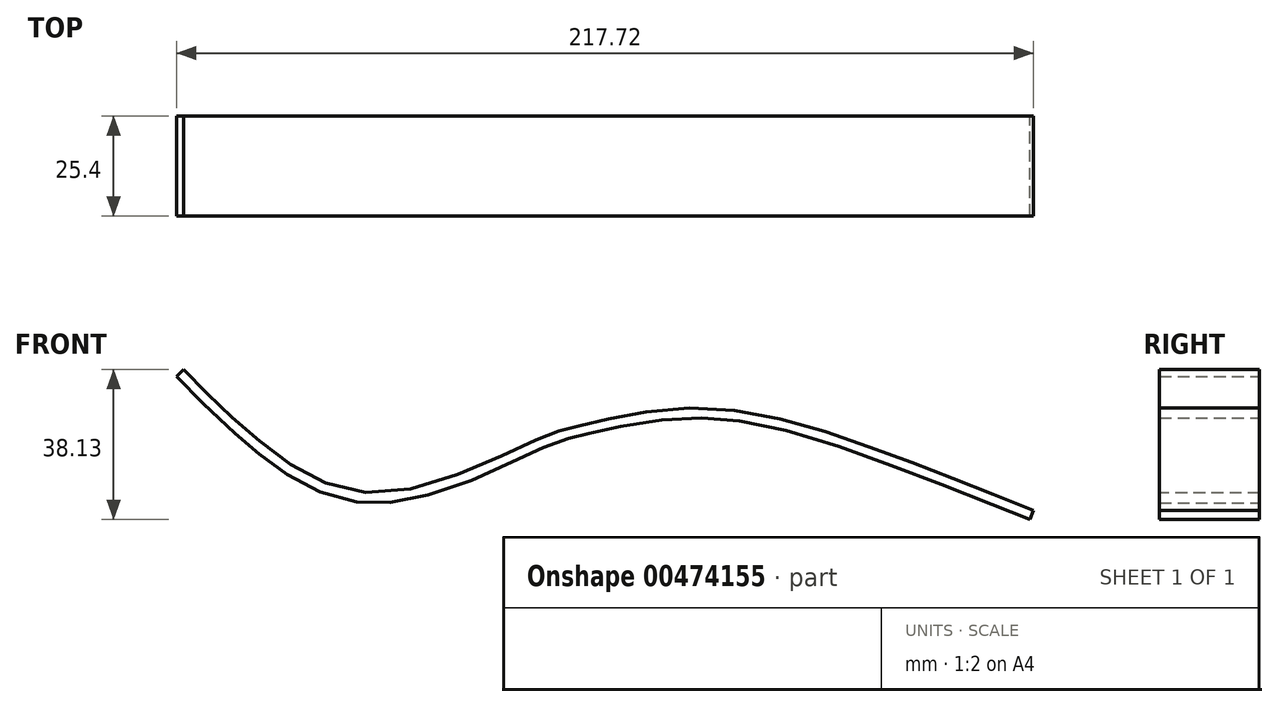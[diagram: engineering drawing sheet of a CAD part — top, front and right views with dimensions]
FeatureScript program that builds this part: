
annotation { "Feature Type Name" : "Feature", "Feature Type Description" : "" }
export const myFeature = defineFeature(function(context is Context, id is Id, definition is map)
    precondition{}
    {
        {
            var Q0;
            Q0=qCreatedBy(makeId("Front.planeOp"),FACE);
            var sketch = newSketch(context, id + "F0", { "sketchPlane" : qUnion([Q0])});
            skFitSpline(sketch, "E0", {"points": [v(0, 0) * mm, v(19, -18.04) * mm, v(50.02, -31.34) * mm, v(90.54, -17.41) * mm, v(100.67, -14.25) * mm, v(131.7, -9.81) * mm, v(176.65, -20.58) * mm, v(215.9, -35.77) * mm], "startDerivative": vector(136.1, -139.5) * mm, "endDerivative": vector(233.57, -93.12) * mm});
            skFitSpline(sketch, "E1.0", {"points": [v(-1.82, -1.77) * mm, v(-0.4, -3.23) * mm, v(2.44, -6.14) * mm, v(6.85, -10.54) * mm, v(10.75, -14.22) * mm, v(14.05, -17.18) * mm, v(16.2, -19.03) * mm, v(18, -20.51) * mm, v(19.83, -22) * mm, v(22.22, -23.84) * mm, v(25.25, -25.98) * mm, v(28.44, -27.99) * mm, v(31.82, -29.8) * mm, v(35.39, -31.37) * mm, v(39.15, -32.62) * mm, v(43.1, -33.5) * mm, v(46.56, -33.87) * mm, v(49.42, -33.92) * mm, v(52.34, -33.79) * mm, v(56.04, -33.31) * mm, v(60.52, -32.35) * mm, v(64.98, -31.06) * mm, v(70.85, -29.04) * mm, v(76.47, -26.7) * mm, v(81.62, -24.37) * mm, v(85.17, -22.7) * mm, v(88.36, -21.2) * mm, v(91.1, -19.93) * mm, v(93.29, -19) * mm, v(95.09, -18.33) * mm, v(96.7, -17.83) * mm, v(98.05, -17.48) * mm, v(99.23, -17.2) * mm, v(100.2, -16.97) * mm, v(101.25, -16.72) * mm, v(102.8, -16.35) * mm, v(104.93, -15.84) * mm, v(107.82, -15.18) * mm, v(110.98, -14.5) * mm, v(115.51, -13.64) * mm, v(120.44, -12.9) * mm, v(125.6, -12.46) * mm, v(129.53, -12.3) * mm, v(133.48, -12.37) * mm, v(137.47, -12.67) * mm, v(141.49, -13.18) * mm, v(146.87, -14.1) * mm, v(153.64, -15.67) * mm, v(161.75, -18.06) * mm, v(169.79, -20.78) * mm, v(177.69, -23.65) * mm, v(185.39, -26.53) * mm, v(192.92, -29.42) * mm, v(200.33, -32.32) * mm, v(207.66, -35.22) * mm, v(212.53, -37.16) * mm, v(214.96, -38.13) * mm]});
            skLineSegment(sketch, "E2", {"start": v(0, 0) * mm, "end": v(-1.82, -1.77) * mm});
            skLineSegment(sketch, "E3", {"start": v(215.9, -35.77) * mm, "end": v(214.96, -38.13) * mm});
            skSolve(sketch);
        }
        {
            var Q0;
            Q0 = qSketchRegion(id + "F0", true);
            extrude(context, id + "F1", {"entities" : qUnion([Q0]), "endBound" : BoundingType.SYMMETRIC, "depth" : 25.4 * mm});
        }
    });
